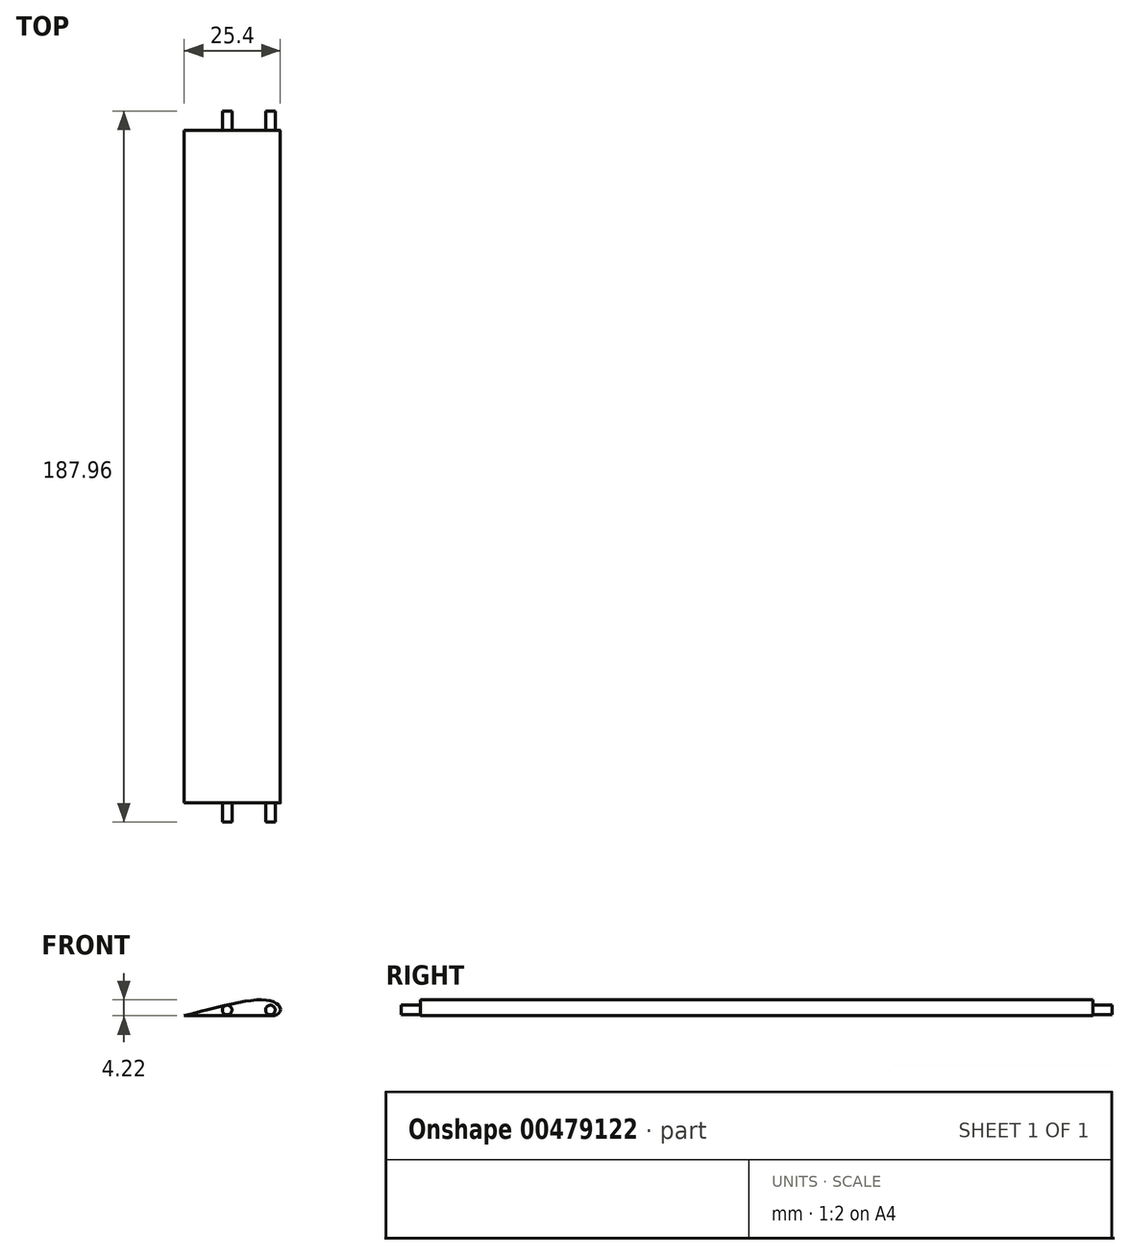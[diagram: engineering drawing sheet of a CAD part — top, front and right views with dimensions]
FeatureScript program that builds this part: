
annotation { "Feature Type Name" : "Feature", "Feature Type Description" : "" }
export const myFeature = defineFeature(function(context is Context, id is Id, definition is map)
    precondition{}
    {
        {
            var Q0;
            Q0=qCreatedBy(makeId("Front.planeOp"),FACE);
            var sketch = newSketch(context, id + "F0", { "sketchPlane" : qUnion([Q0])});
            skLineSegment(sketch, "E0", {"start": v(-11.02, 0) * mm, "end": v(11.95, 0) * mm});
            skFitSpline(sketch, "E1", {"points": [v(11.95, 0) * mm, v(14.38, 1.57) * mm, v(11.95, 3.9) * mm, v(-11.02, 0) * mm], "startDerivative": vector(20.76, 0) * mm, "endDerivative": vector(-51.78, -13.79) * mm});
            skCircle(sketch, "E2", {"center": v(11.73, 1.52) * mm, "radius": 1.27 * mm});
            skCircle(sketch, "E3", {"center": v(0.3, 1.52) * mm, "radius": 1.27 * mm});
            skSolve(sketch);
        }
        {
            var Q0;
            Q0 = qSketchRegion(id + "F0", true);
            var Q1;
            Q1=makeQuery(id+"F0.imprint","IMPRINT",FACE,{"disambiguationData":[TD([[makeQuery(id+"F0.imprint","IMPRINT",EDGE,{"derivedFrom":sQuery(id+"F0.wireOp",EDGE,"E3")}),1.0]])]});
            var Q2;
            Q2=makeQuery(id+"F0.imprint","IMPRINT",FACE,{"disambiguationData":[TD([[makeQuery(id+"F0.imprint","IMPRINT",EDGE,{"derivedFrom":sQuery(id+"F0.wireOp",EDGE,"E2")}),1.0]])]});
            extrude(context, id + "F1", {"entities" : qUnion([Q0, Q1, Q2]), "depth" : 177.8 * mm});
        }
        {
            var Q0;
            Q0=makeQuery(id+"F0.imprint","IMPRINT",FACE,{"disambiguationData":[TD([[makeQuery(id+"F0.imprint","IMPRINT",EDGE,{"derivedFrom":sQuery(id+"F0.wireOp",EDGE,"E2")}),1.0]])]});
            var Q1;
            Q1=makeQuery(id+"F0.imprint","IMPRINT",FACE,{"disambiguationData":[TD([[makeQuery(id+"F0.imprint","IMPRINT",EDGE,{"derivedFrom":sQuery(id+"F0.wireOp",EDGE,"E3")}),1.0]])]});
            extrude(context, id + "F2", {"entities" : qUnion([Q0, Q1]), "operationType" : NewBodyOperationType.ADD, "oppositeDirection" : true, "depth" : 5.08 * mm});
        }
        {
            var Q0;
            Q0=makeQuery(id+"F0.imprint","IMPRINT",FACE,{"disambiguationData":[TD([[makeQuery(id+"F0.imprint","IMPRINT",EDGE,{"derivedFrom":sQuery(id+"F0.wireOp",EDGE,"E3")}),1.0]])]});
            var Q1;
            Q1=makeQuery(id+"F0.imprint","IMPRINT",FACE,{"disambiguationData":[TD([[makeQuery(id+"F0.imprint","IMPRINT",EDGE,{"derivedFrom":sQuery(id+"F0.wireOp",EDGE,"E2")}),1.0]])]});
            extrude(context, id + "F3", {"entities" : qUnion([Q0, Q1]), "operationType" : NewBodyOperationType.ADD, "depth" : 182.88 * mm});
        }
    });
